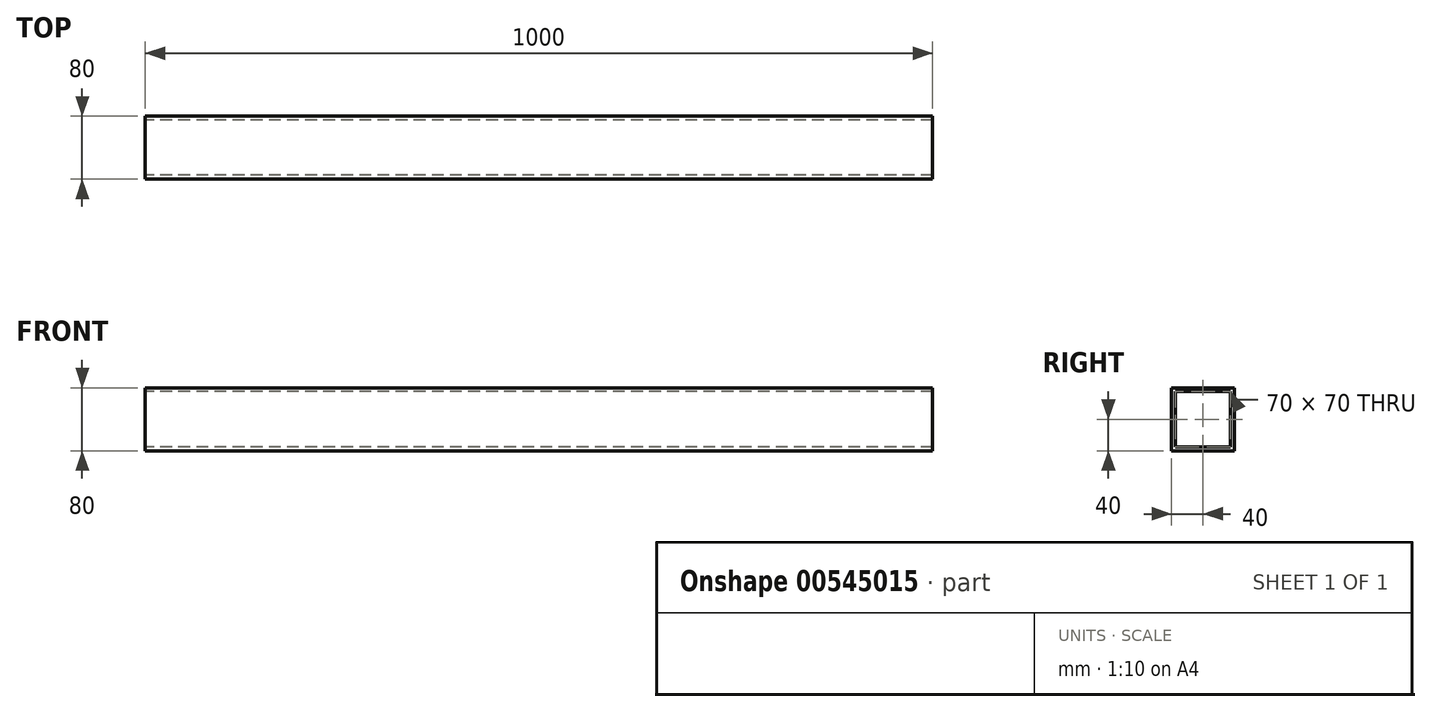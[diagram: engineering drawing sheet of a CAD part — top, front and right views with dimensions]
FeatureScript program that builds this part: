
annotation { "Feature Type Name" : "Feature", "Feature Type Description" : "" }
export const myFeature = defineFeature(function(context is Context, id is Id, definition is map)
    precondition{}
    {
        {
            var Q0;
            Q0=qCreatedBy(makeId("Right.planeOp"),FACE);
            var sketch = newSketch(context, id + "F0", { "sketchPlane" : qUnion([Q0])});
            skLineSegment(sketch, "E0.bottom", {"start": v(40, 40) * mm, "end": v(-40, 40) * mm});
            skLineSegment(sketch, "E0.top", {"start": v(40, -40) * mm, "end": v(-40, -40) * mm});
            skLineSegment(sketch, "E0.left", {"start": v(40, 40) * mm, "end": v(40, -40) * mm});
            skLineSegment(sketch, "E0.right", {"start": v(-40, 40) * mm, "end": v(-40, -40) * mm});
            skPoint(sketch, "E0.middle", {"position": v(0, 0) * mm});
            skLineSegment(sketch, "E1.bottom", {"start": v(-35, 35) * mm, "end": v(35, 35) * mm});
            skLineSegment(sketch, "E1.top", {"start": v(-35, -35) * mm, "end": v(35, -35) * mm});
            skLineSegment(sketch, "E1.left", {"start": v(-35, 35) * mm, "end": v(-35, -35) * mm});
            skLineSegment(sketch, "E1.right", {"start": v(35, 35) * mm, "end": v(35, -35) * mm});
            skSolve(sketch);
        }
        {
            var Q0;
            Q0=makeQuery(id+"F0.imprint","IMPRINT",FACE,{"disambiguationData":[TD([[makeQuery(id+"F0.imprint","IMPRINT",EDGE,{"derivedFrom":sQuery(id+"F0.wireOp",EDGE,"E0.bottom")}),1.0]])]});
            extrude(context, id + "F1", {"entities" : qUnion([Q0]), "endBound" : BoundingType.SYMMETRIC, "depth" : 1000 * mm, "offsetDistance" : 25 * mm});
        }
    });
